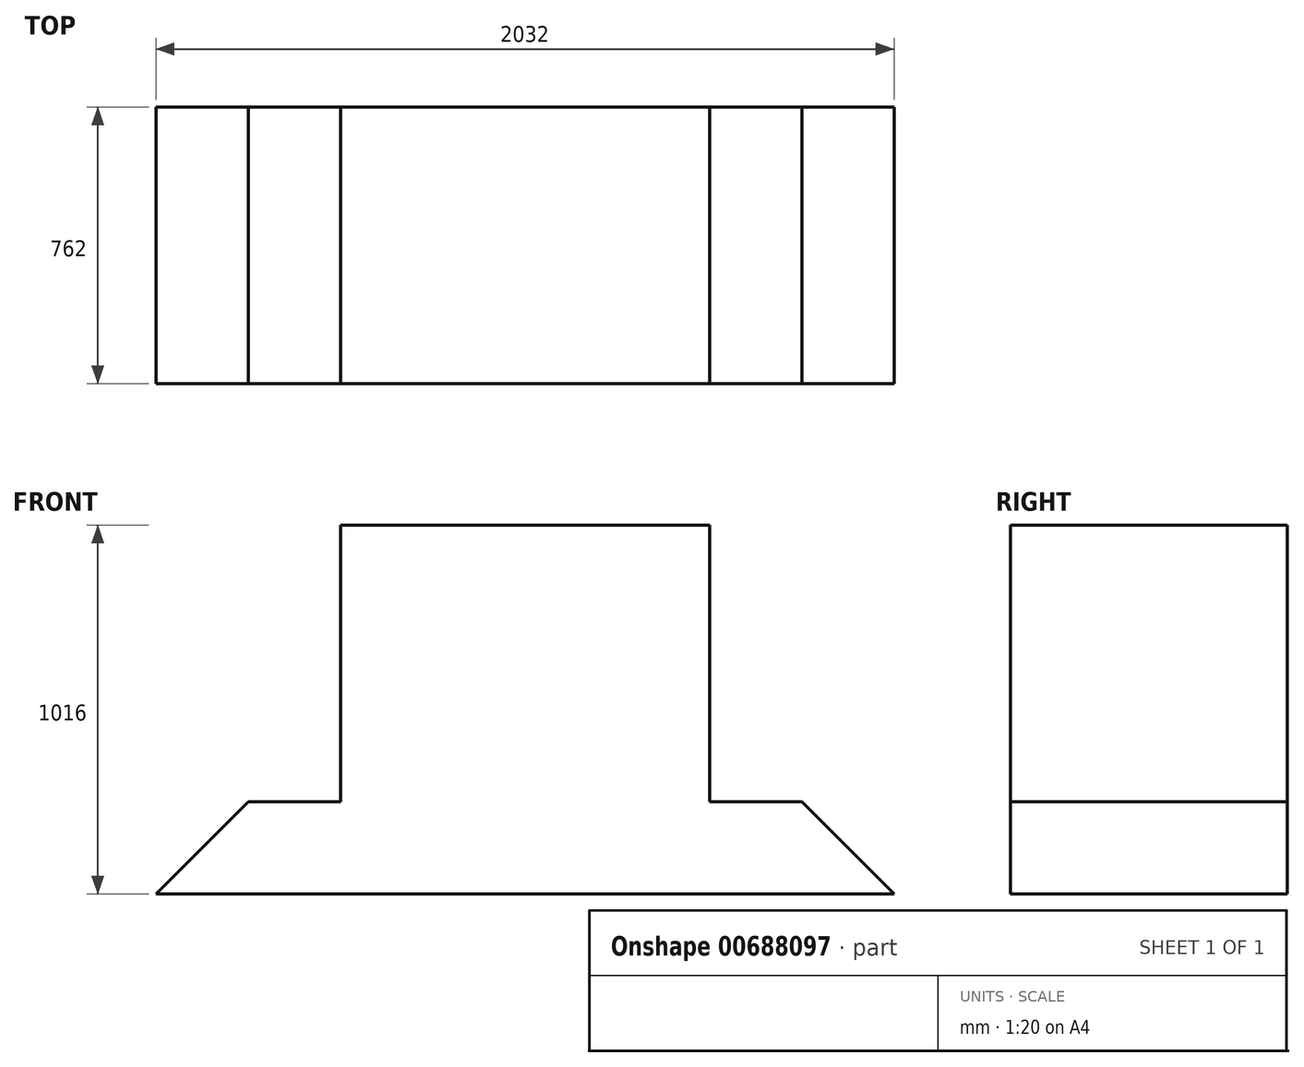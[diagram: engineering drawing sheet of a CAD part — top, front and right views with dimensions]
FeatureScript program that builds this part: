
annotation { "Feature Type Name" : "Feature", "Feature Type Description" : "" }
export const myFeature = defineFeature(function(context is Context, id is Id, definition is map)
    precondition{}
    {
        {
            var Q0;
            Q0=qCreatedBy(makeId("Front.planeOp"),FACE);
            var sketch = newSketch(context, id + "F0", { "sketchPlane" : qUnion([Q0])});
            skLineSegment(sketch, "E0", {"start": v(0, 0) * mm, "end": v(2032, 0) * mm});
            skLineSegment(sketch, "E1", {"start": v(2032, 0) * mm, "end": v(1778, 254) * mm});
            skLineSegment(sketch, "E2", {"start": v(1778, 254) * mm, "end": v(1524, 254) * mm});
            skLineSegment(sketch, "E3", {"start": v(1524, 254) * mm, "end": v(1524, 1016) * mm});
            skLineSegment(sketch, "E4", {"start": v(1524, 1016) * mm, "end": v(508, 1016) * mm});
            skLineSegment(sketch, "E5", {"start": v(508, 1016) * mm, "end": v(508, 254) * mm});
            skLineSegment(sketch, "E6", {"start": v(508, 254) * mm, "end": v(254, 254) * mm});
            skLineSegment(sketch, "E7", {"start": v(254, 254) * mm, "end": v(0, 0) * mm});
            skSolve(sketch);
        }
        {
            var Q0;
            Q0=makeQuery(id+"F0.imprint","IMPRINT",FACE,{"disambiguationData":[TD([[makeQuery(id+"F0.imprint","IMPRINT",EDGE,{"derivedFrom":sQuery(id+"F0.wireOp",EDGE,"E0")}),1.0]])]});
            extrude(context, id + "F1", {"entities" : qUnion([Q0]), "depth" : 762 * mm, "offsetDistance" : 25.4 * mm});
        }
    });
